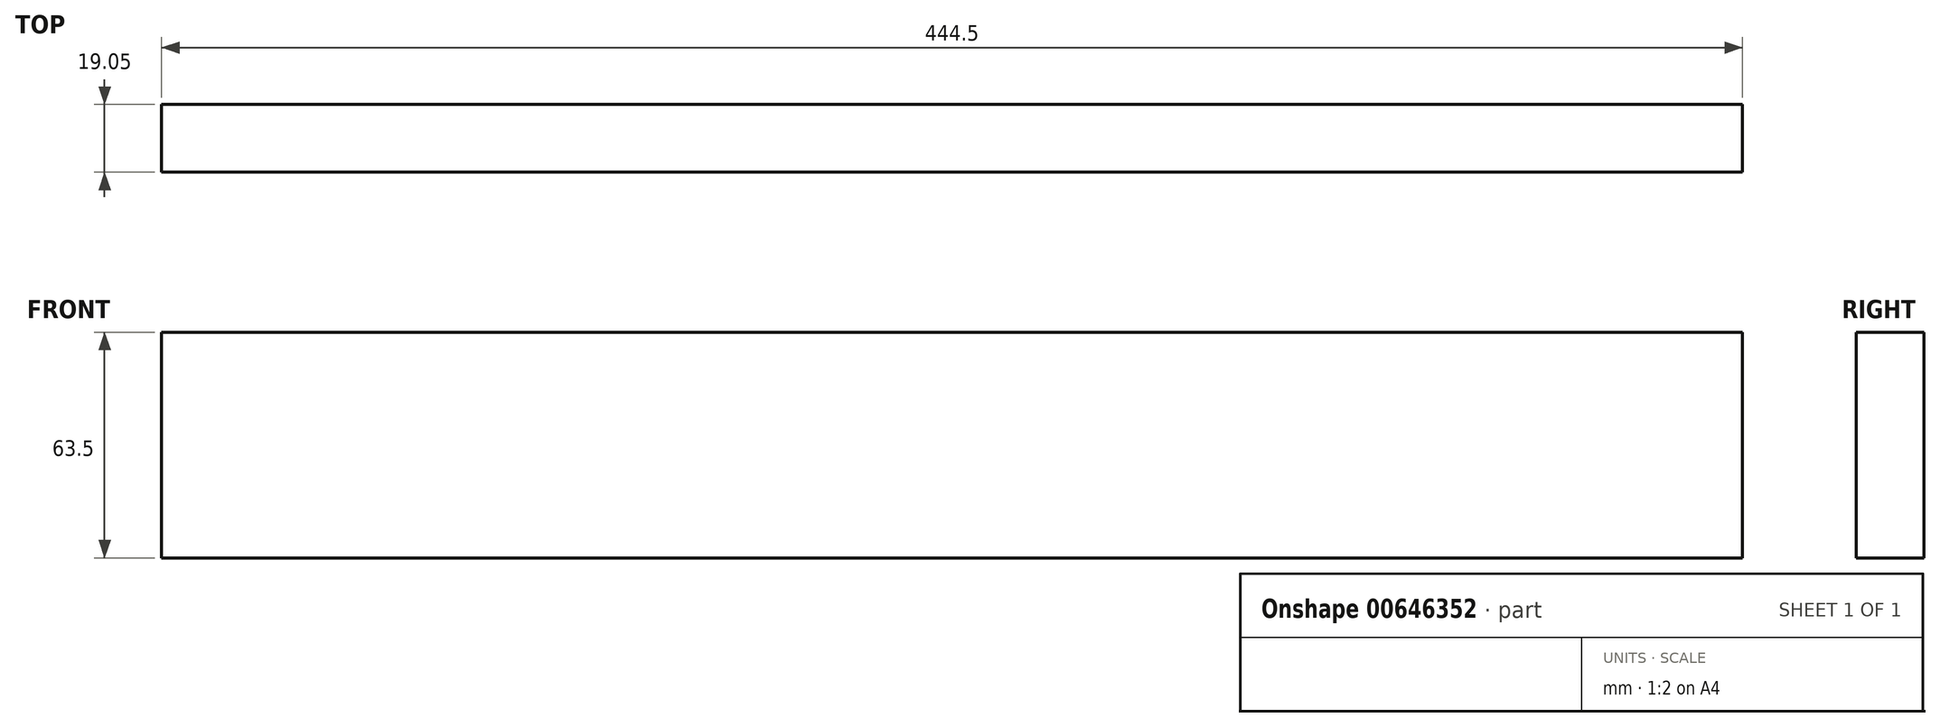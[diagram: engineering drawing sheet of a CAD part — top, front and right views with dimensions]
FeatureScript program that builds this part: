
annotation { "Feature Type Name" : "Feature", "Feature Type Description" : "" }
export const myFeature = defineFeature(function(context is Context, id is Id, definition is map)
    precondition{}
    {
        {
            var Q0;
            Q0=qCreatedBy(makeId("Front.planeOp"),FACE);
            var sketch = newSketch(context, id + "F0", { "sketchPlane" : qUnion([Q0])});
            skLineSegment(sketch, "E0.bottom", {"start": v(222.25, -31.75) * mm, "end": v(-222.25, -31.75) * mm});
            skLineSegment(sketch, "E0.top", {"start": v(222.25, 31.75) * mm, "end": v(-222.25, 31.75) * mm});
            skLineSegment(sketch, "E0.left", {"start": v(222.25, -31.75) * mm, "end": v(222.25, 31.75) * mm});
            skLineSegment(sketch, "E0.right", {"start": v(-222.25, -31.75) * mm, "end": v(-222.25, 31.75) * mm});
            skPoint(sketch, "E0.middle", {"position": v(0, 0) * mm});
            skSolve(sketch);
        }
        {
            var Q0;
            Q0=makeQuery(id+"F0.imprint","IMPRINT",FACE,{"disambiguationData":[TD([[makeQuery(id+"F0.imprint","IMPRINT",EDGE,{"derivedFrom":sQuery(id+"F0.wireOp",EDGE,"E0.bottom")}),-1.0]])]});
            extrude(context, id + "F1", {"entities" : qUnion([Q0]), "oppositeDirection" : true, "depth" : 19.05 * mm, "offsetDistance" : 25.4 * mm});
        }
    });
